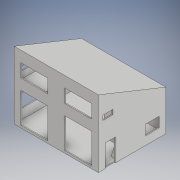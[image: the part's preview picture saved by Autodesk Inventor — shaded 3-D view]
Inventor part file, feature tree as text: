
AUTODESK INVENTOR PART (.ipt)
format: ipt  version: 2017 (Build 210142000, 142)  size: 328,192 bytes
history: native  units: in
note: dims shown in document units (in); Inventor stores cm internally (conversion verified against a paired STEP export)
features: sketch x18, extrude x17, plane x3, shell x1
ambient origin geometry x8: Origin, YZ Plane, XZ Plane, XY Plane, X Axis, Y Axis, Z Axis, Center Point
bodies: Solid1 (feature_tree)
feature tree (39):
  extrude  "main body"  Depth=240.0in
  extrude  "triangle"  Depth=96.0in
  shell  "Shell1"  Thickness=300.0in
  plane  "Work Plane1"
  extrude  "second floor"  Depth=96.0in
  plane  "Work Plane3"
  extrude  "bedroom"  Depth=6.0in TaperAngle=0.0deg
  extrude  "upper stairs"  TaperAngle=0.0deg  [1 undecoded]
  extrude  "main stairs"  Depth=84.0in
  sketch  "Sketch18"  dims[d21=6.0in d22=0.0in d23=0.0in]
  plane  "Work Plane4"
  extrude  "room wall 1"  TaperAngle=0.0deg  [1 undecoded]
  extrude  "room wall 2"  Depth=36.0in
  extrude  "outer wall"  Depth=24.0in TaperAngle=0.0deg
  sketch  "Sketch24"  dims[d52=54.0in d53=2.0in d54=0.0in]
  extrude  "side window 1"  Depth=24.0in TaperAngle=0.0deg
  sketch  "Sketch30"  dims[d73=8.0in d74=24.0in]
  extrude  "my WALL"  Depth=2.0in TaperAngle=0.0deg
  extrude  "other side window 1"  Depth=2.0in TaperAngle=0.0deg
  extrude  "front bottom windows"  Depth=96.0in
  extrude  "front top windows"  Depth=108.0in
  extrude  "Extrusion27"  Depth=24.0in
  extrude  "Extrusion28"  Depth=16.135in
  extrude  "Extrusion29"  Depth=12.0in TaperAngle=0.0deg
  sketch  "Sketch1"  dims[d0=300.0in d1=240.0in]
  sketch  "Sketch3"  dims[d2=144.0in d3=0.0in d4=96.0in d5=300.0in d6=0.0in]
  sketch  "Sketch6"  dims[d7=3.5in d8=96.0in]
  sketch  "Sketch8"  dims[d12=120.0in d13=6.0in d14=0.0in]
  sketch  "Sketch16"  dims[d16=24.0in d17=0.0in]
  sketch  "Sketch17"  dims[d19=0.0in d20=84.0in]
  sketch  "Sketch20"  dims[d39=24.0in d40=36.0in]
  sketch  "Sketch21"  dims[d42=0.0in d43=24.0in d44=0.0in]
  sketch  "Sketch23"  dims[d46=0.7902in d48=24.0in d49=0.0in]
  sketch  "Sketch26"  dims[d56=2.0in d57=0.0in d60=1.0in d61=0.0in]
  sketch  "Sketch28"  dims[d62=8.0in d63=96.0in]
  sketch  "Sketch29"  dims[d64=24.0in d65=108.0in]
  sketch  "Sketch31"  dims[d78=36.0in d79=16.135in]
  sketch  "Sketch32"  dims[d81=12.0in d82=1.0in d83=0.0in]
  sketch  "Sketch33"  dims[d95=24.0in d100=3.5in d101=0.0in d102=3.5in d103=0.0in d105=96.0in d106=24.0in d107=24.0in d118=48.0in d119=0.7874in d121=156.0in d122=0.3937in d124=12.0in d126=3.5in d127=0.0in d130=3.5in d131=0.0in d132=48.0in d133=72.0in d134=38.0in d135=24.0in d136=24.0in d137=38.0in d138=1.0in d139=0.0in d140=80.0in d141=36.0in d142=24.0in d143=3.5in d144=0.0in d145=48.0in d146=36.0in d147=24.0in d148=30.0in d149=1.0in d150=0.0in]
note: 2 required parameter values undecoded (feature->parameter linkage not recoverable at this tier; creation-order binding heuristic only, values carry confidence <= 0.55)
